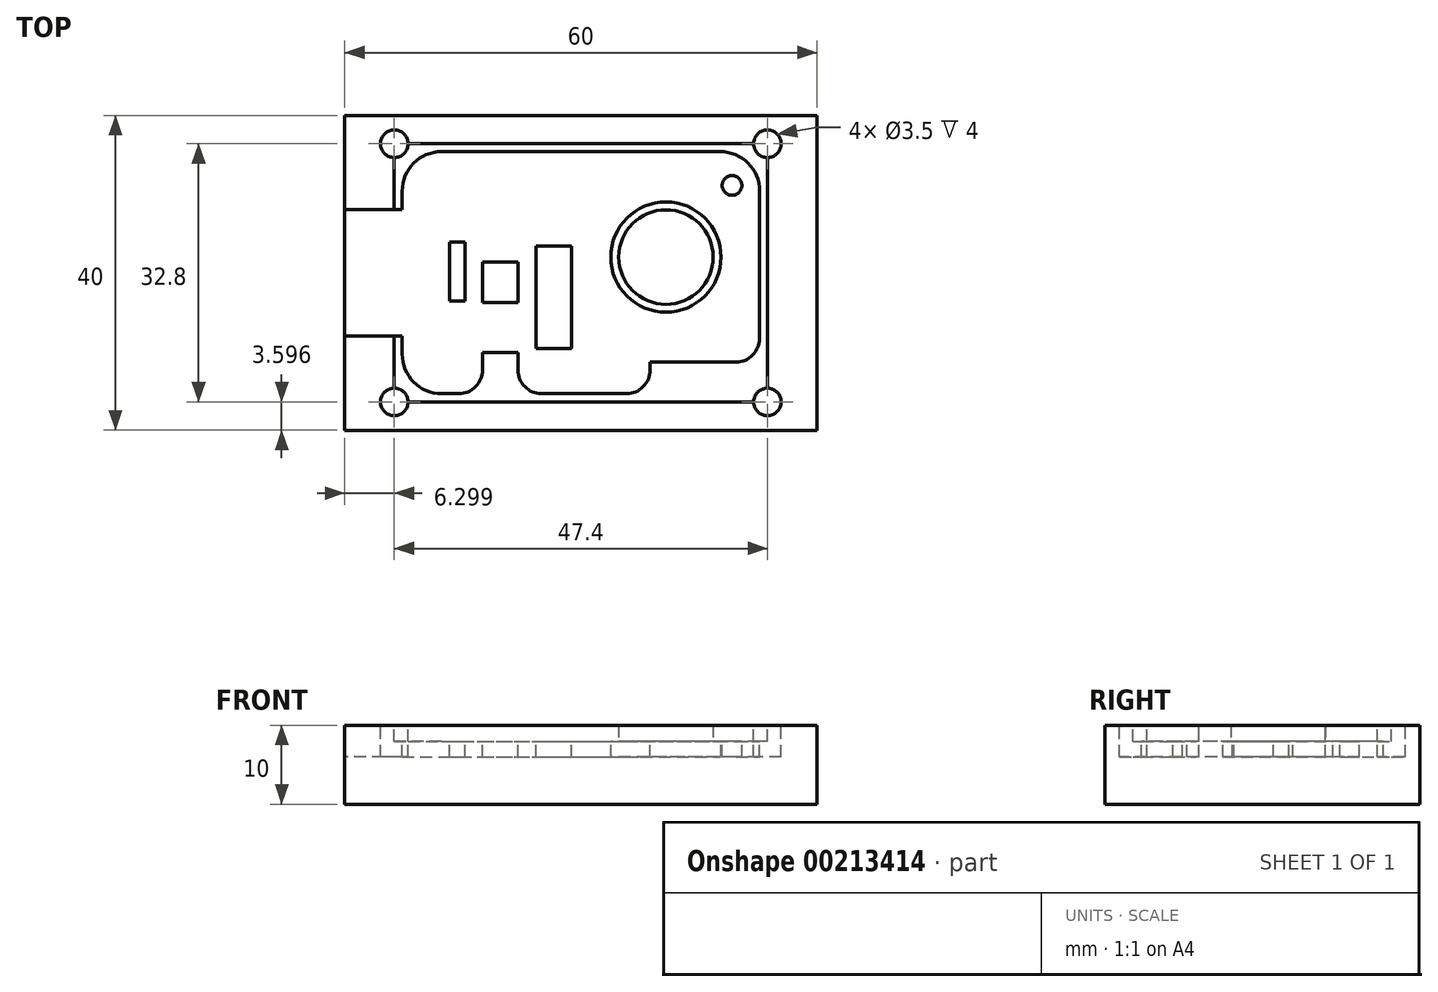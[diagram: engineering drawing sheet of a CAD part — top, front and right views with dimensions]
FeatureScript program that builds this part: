
annotation { "Feature Type Name" : "Feature", "Feature Type Description" : "" }
export const myFeature = defineFeature(function(context is Context, id is Id, definition is map)
    precondition{}
    {
        {
            var Q0;
            Q0=qCreatedBy(makeId("Top.planeOp"),FACE);
            var sketch = newSketch(context, id + "F0", { "sketchPlane" : qUnion([Q0])});
            skLineSegment(sketch, "E0.bottom", {"start": v(30.43, -28.68) * mm, "end": v(90.43, -28.68) * mm});
            skLineSegment(sketch, "E0.top", {"start": v(30.43, -68.68) * mm, "end": v(90.43, -68.68) * mm});
            skLineSegment(sketch, "E0.left", {"start": v(30.43, -28.68) * mm, "end": v(30.43, -68.68) * mm});
            skLineSegment(sketch, "E0.right", {"start": v(90.43, -28.68) * mm, "end": v(90.43, -68.68) * mm});
            skSolve(sketch);
        }
        {
            var Q0;
            Q0=makeQuery(id+"F0.imprint","IMPRINT",FACE,{"disambiguationData":[TD([[makeQuery(id+"F0.imprint","IMPRINT",EDGE,{"derivedFrom":sQuery(id+"F0.wireOp",EDGE,"E0.bottom")}),-1.0]])]});
            extrude(context, id + "F1", {"entities" : qUnion([Q0]), "depth" : 10 * mm});
        }
        {
            var Q0;
            Q0=makeQuery(id+"F1.opExtrude","CAP_FACE",FACE,{"disambiguationData":[OSD([sQuery(id+"F0.wireOp",EDGE,"E0.bottom"),sQuery(id+"F0.wireOp",EDGE,"E0.top"),sQuery(id+"F0.wireOp",EDGE,"E0.left"),sQuery(id+"F0.wireOp",EDGE,"E0.right")])],"isStart":false});
            var sketch = newSketch(context, id + "F2", { "sketchPlane" : qUnion([Q0])});
            skLineSegment(sketch, "E1.bottom", {"start": v(36.73, -32.28) * mm, "end": v(84.13, -32.28) * mm});
            skLineSegment(sketch, "E1.top", {"start": v(36.73, -65.08) * mm, "end": v(84.13, -65.08) * mm});
            skLineSegment(sketch, "E1.left", {"start": v(36.73, -32.28) * mm, "end": v(36.73, -65.08) * mm});
            skLineSegment(sketch, "E1.right", {"start": v(84.13, -32.28) * mm, "end": v(84.13, -65.08) * mm});
            skCircle(sketch, "E2", {"center": v(36.73, -32.28) * mm, "radius": 1.75 * mm});
            skCircle(sketch, "E3", {"center": v(84.13, -65.08) * mm, "radius": 1.75 * mm});
            skCircle(sketch, "E4", {"center": v(84.13, -32.28) * mm, "radius": 1.75 * mm});
            skCircle(sketch, "E5", {"center": v(36.73, -65.08) * mm, "radius": 1.75 * mm});
            skLineSegment(sketch, "E6.bottom", {"start": v(38.7, -40.66) * mm, "end": v(22.17, -40.66) * mm});
            skLineSegment(sketch, "E6.top", {"start": v(38.7, -56.7) * mm, "end": v(22.17, -56.7) * mm});
            skLineSegment(sketch, "E6.left", {"start": v(38.7, -40.66) * mm, "end": v(38.7, -56.7) * mm});
            skLineSegment(sketch, "E6.right", {"start": v(22.17, -40.66) * mm, "end": v(22.17, -56.7) * mm});
            skPoint(sketch, "E6.middle", {"position": v(30.43, -48.68) * mm});
            skSolve(sketch);
        }
        {
            var Q0;
            {var subQ0=sQuery(id+"F2.wireOp",EDGE,"E1.left");var subQ1=sQuery(id+"F2.wireOp",EDGE,"E1.bottom");var subQ2=makeQuery(id+"F2.imprint","INTERSECT",VERTEX,{"derivedFrom":[subQ1,subQ0]});Q0=makeQuery(id+"F2.imprint","IMPRINT",FACE,{"disambiguationData":[TD([[makeQuery(id+"F2.imprint","IMPRINT",EDGE,{"disambiguationData":[TD([[subQ2,-1.0]])],"derivedFrom":subQ1}),-1.0]])]});}
            var Q1;
            {var subQ0=sQuery(id+"F2.wireOp",EDGE,"E1.left");var subQ1=sQuery(id+"F2.wireOp",EDGE,"E1.bottom");var subQ2=makeQuery(id+"F2.imprint","INTERSECT",VERTEX,{"derivedFrom":[subQ1,subQ0]});Q1=makeQuery(id+"F2.imprint","IMPRINT",FACE,{"disambiguationData":[TD([[makeQuery(id+"F2.imprint","IMPRINT",EDGE,{"disambiguationData":[TD([[subQ2,-1.0]])],"derivedFrom":subQ1}),1.0]])]});}
            var Q2;
            {var subQ0=sQuery(id+"F2.wireOp",EDGE,"E1.left");var subQ1=sQuery(id+"F2.wireOp",EDGE,"E1.top");var subQ2=makeQuery(id+"F2.imprint","INTERSECT",VERTEX,{"derivedFrom":[subQ1,subQ0]});Q2=makeQuery(id+"F2.imprint","IMPRINT",FACE,{"disambiguationData":[TD([[makeQuery(id+"F2.imprint","IMPRINT",EDGE,{"disambiguationData":[TD([[subQ2,-1.0]])],"derivedFrom":subQ1}),1.0]])]});}
            var Q3;
            {var subQ0=sQuery(id+"F2.wireOp",EDGE,"E1.left");var subQ1=sQuery(id+"F2.wireOp",EDGE,"E1.top");var subQ2=makeQuery(id+"F2.imprint","INTERSECT",VERTEX,{"derivedFrom":[subQ1,subQ0]});Q3=makeQuery(id+"F2.imprint","IMPRINT",FACE,{"disambiguationData":[TD([[makeQuery(id+"F2.imprint","IMPRINT",EDGE,{"disambiguationData":[TD([[subQ2,-1.0]])],"derivedFrom":subQ1}),-1.0]])]});}
            var Q4;
            {var subQ0=sQuery(id+"F2.wireOp",EDGE,"E1.right");var subQ1=sQuery(id+"F2.wireOp",EDGE,"E1.top");var subQ2=makeQuery(id+"F2.imprint","INTERSECT",VERTEX,{"derivedFrom":[subQ1,subQ0]});Q4=makeQuery(id+"F2.imprint","IMPRINT",FACE,{"disambiguationData":[TD([[makeQuery(id+"F2.imprint","IMPRINT",EDGE,{"disambiguationData":[TD([[subQ2,1.0]])],"derivedFrom":subQ1}),-1.0]])]});}
            var Q5;
            {var subQ0=sQuery(id+"F2.wireOp",EDGE,"E1.right");var subQ1=sQuery(id+"F2.wireOp",EDGE,"E1.top");var subQ2=makeQuery(id+"F2.imprint","INTERSECT",VERTEX,{"derivedFrom":[subQ1,subQ0]});Q5=makeQuery(id+"F2.imprint","IMPRINT",FACE,{"disambiguationData":[TD([[makeQuery(id+"F2.imprint","IMPRINT",EDGE,{"disambiguationData":[TD([[subQ2,1.0]])],"derivedFrom":subQ1}),1.0]])]});}
            var Q6;
            {var subQ0=sQuery(id+"F2.wireOp",EDGE,"E2");var subQ13=sQuery(id+"F2.wireOp",EDGE,"E1.bottom");var subQ15=makeQuery(id+"F2.imprint","INTERSECT",VERTEX,{"derivedFrom":[subQ13,subQ0]});Q6=makeQuery(id+"F2.imprint","IMPRINT",FACE,{"disambiguationData":[TD([[makeQuery(id+"F2.imprint","IMPRINT",EDGE,{"disambiguationData":[TD([[subQ15,-1.0]])],"derivedFrom":subQ13}),-1.0]])]});}
            var Q7;
            {var subQ0=sQuery(id+"F2.wireOp",EDGE,"E1.right");var subQ1=sQuery(id+"F2.wireOp",EDGE,"E1.bottom");var subQ2=makeQuery(id+"F2.imprint","INTERSECT",VERTEX,{"derivedFrom":[subQ1,subQ0]});Q7=makeQuery(id+"F2.imprint","IMPRINT",FACE,{"disambiguationData":[TD([[makeQuery(id+"F2.imprint","IMPRINT",EDGE,{"disambiguationData":[TD([[subQ2,1.0]])],"derivedFrom":subQ1}),-1.0]])]});}
            var Q8;
            {var subQ0=sQuery(id+"F2.wireOp",EDGE,"E1.right");var subQ1=sQuery(id+"F2.wireOp",EDGE,"E1.bottom");var subQ2=makeQuery(id+"F2.imprint","INTERSECT",VERTEX,{"derivedFrom":[subQ1,subQ0]});Q8=makeQuery(id+"F2.imprint","IMPRINT",FACE,{"disambiguationData":[TD([[makeQuery(id+"F2.imprint","IMPRINT",EDGE,{"disambiguationData":[TD([[subQ2,1.0]])],"derivedFrom":subQ1}),1.0]])]});}
            extrude(context, id + "F3", {"entities" : qUnion([Q0, Q1, Q2, Q3, Q4, Q5, Q6, Q7, Q8]), "operationType" : NewBodyOperationType.REMOVE, "oppositeDirection" : true, "depth" : 2 * mm});
        }
        {
            var Q0;
            Q0=makeQuery(id+"F3.boolean.opBoolean","COPY",FACE,{"derivedFrom":makeQuery(id+"F3.opExtrude","CAP_FACE",FACE,{"disambiguationData":[OSD([sQuery(id+"F2.wireOp",EDGE,"E1.bottom"),sQuery(id+"F2.wireOp",EDGE,"E1.top"),sQuery(id+"F2.wireOp",EDGE,"E1.left"),sQuery(id+"F2.wireOp",EDGE,"E1.right"),sQuery(id+"F2.wireOp",EDGE,"E2"),sQuery(id+"F2.wireOp",EDGE,"E3"),sQuery(id+"F2.wireOp",EDGE,"E4"),sQuery(id+"F2.wireOp",EDGE,"E5")])],"isStart":false})});
            var sketch = newSketch(context, id + "F4", { "sketchPlane" : qUnion([Q0])});
            skCircle(sketch, "E7", {"center": v(71.23, -46.68) * mm, "radius": 6 * mm});
            skCircle(sketch, "E8", {"center": v(79.63, -37.58) * mm, "radius": 1.25 * mm});
            skLineSegment(sketch, "E9.bottom", {"start": v(42.73, -33.28) * mm, "end": v(78.13, -33.28) * mm});
            skLineSegment(sketch, "E9.left", {"start": v(37.73, -38.28) * mm, "end": v(37.73, -59.03) * mm});
            skLineSegment(sketch, "E9.right", {"start": v(83.13, -38.28) * mm, "end": v(83.13, -57.03) * mm});
            skLineSegment(sketch, "E10.bottom", {"start": v(47.93, -47.28) * mm, "end": v(52.43, -47.28) * mm});
            skLineSegment(sketch, "E10.top", {"start": v(47.93, -52.48) * mm, "end": v(52.43, -52.48) * mm});
            skLineSegment(sketch, "E10.left", {"start": v(47.93, -47.28) * mm, "end": v(47.93, -52.48) * mm});
            skLineSegment(sketch, "E10.right", {"start": v(52.43, -47.28) * mm, "end": v(52.43, -52.48) * mm});
            skLineSegment(sketch, "E11.bottom", {"start": v(47.93, -58.83) * mm, "end": v(52.43, -58.83) * mm});
            skLineSegment(sketch, "E11.left", {"start": v(47.93, -58.83) * mm, "end": v(47.93, -61.03) * mm});
            skLineSegment(sketch, "E11.right", {"start": v(52.43, -58.83) * mm, "end": v(52.43, -61.03) * mm});
            skPoint(sketch, "E12.visualSharp", {"position": v(37.73, -33.28) * mm});
            skArc(sketch, "E12.filletArc", {"start": v(42.73, -33.28) * mm, "mid": v(39.2, -34.75) * mm, "end": v(37.73, -38.28) * mm});
            skPoint(sketch, "E13.visualSharp", {"position": v(83.13, -33.28) * mm});
            skArc(sketch, "E13.filletArc", {"start": v(83.13, -38.28) * mm, "mid": v(81.66, -34.75) * mm, "end": v(78.13, -33.28) * mm});
            skPoint(sketch, "E14.visualSharp", {"position": v(83.13, -64.03) * mm});
            skPoint(sketch, "E15.visualSharp", {"position": v(37.73, -64.03) * mm});
            skArc(sketch, "E15.filletArc", {"start": v(37.73, -59.03) * mm, "mid": v(39.2, -62.56) * mm, "end": v(42.73, -64.03) * mm});
            skLineSegment(sketch, "E16", {"start": v(42.73, -64.03) * mm, "end": v(44.93, -64.03) * mm});
            skPoint(sketch, "E17.visualSharp", {"position": v(47.93, -64.03) * mm});
            skArc(sketch, "E17.filletArc", {"start": v(44.93, -64.03) * mm, "mid": v(47.05, -63.15) * mm, "end": v(47.93, -61.03) * mm});
            skPoint(sketch, "E18.visualSharp", {"position": v(52.43, -64.03) * mm});
            skArc(sketch, "E18.filletArc", {"start": v(52.43, -61.03) * mm, "mid": v(53.3, -63.15) * mm, "end": v(55.43, -64.03) * mm});
            skLineSegment(sketch, "E19.top", {"start": v(80.13, -60.03) * mm, "end": v(69.23, -60.03) * mm});
            skLineSegment(sketch, "E19.right", {"start": v(69.23, -61.03) * mm, "end": v(69.23, -60.03) * mm});
            skLineSegment(sketch, "E20", {"start": v(55.43, -64.03) * mm, "end": v(66.23, -64.03) * mm});
            skLineSegment(sketch, "E21.bottom", {"start": v(54.73, -45.28) * mm, "end": v(59.23, -45.28) * mm});
            skLineSegment(sketch, "E21.top", {"start": v(54.73, -58.28) * mm, "end": v(59.23, -58.28) * mm});
            skLineSegment(sketch, "E21.left", {"start": v(54.73, -45.28) * mm, "end": v(54.73, -58.28) * mm});
            skLineSegment(sketch, "E21.right", {"start": v(59.23, -45.28) * mm, "end": v(59.23, -58.28) * mm});
            skLineSegment(sketch, "E22.bottom", {"start": v(43.73, -44.78) * mm, "end": v(45.73, -44.78) * mm});
            skLineSegment(sketch, "E22.top", {"start": v(43.73, -52.28) * mm, "end": v(45.73, -52.28) * mm});
            skLineSegment(sketch, "E22.left", {"start": v(43.73, -44.78) * mm, "end": v(43.73, -52.28) * mm});
            skLineSegment(sketch, "E22.right", {"start": v(45.73, -44.78) * mm, "end": v(45.73, -52.28) * mm});
            skPoint(sketch, "E23.visualSharp", {"position": v(69.23, -64.03) * mm});
            skArc(sketch, "E23.filletArc", {"start": v(66.23, -64.03) * mm, "mid": v(68.35, -63.15) * mm, "end": v(69.23, -61.03) * mm});
            skPoint(sketch, "E24.visualSharp", {"position": v(83.13, -60.03) * mm});
            skArc(sketch, "E24.filletArc", {"start": v(80.13, -60.03) * mm, "mid": v(82.25, -59.15) * mm, "end": v(83.13, -57.03) * mm});
            skCircle(sketch, "E25", {"center": v(71.23, -46.68) * mm, "radius": 7 * mm});
            skSolve(sketch);
        }
        {
            var Q0;
            {var subQ0=sQuery(id+"F2.wireOp",EDGE,"E1.left");var subQ1=sQuery(id+"F2.wireOp",EDGE,"E1.bottom");var subQ2=makeQuery(id+"F2.imprint","INTERSECT",VERTEX,{"derivedFrom":[subQ1,subQ0]});Q0=makeQuery(id+"F2.imprint","IMPRINT",FACE,{"disambiguationData":[TD([[makeQuery(id+"F2.imprint","IMPRINT",EDGE,{"disambiguationData":[TD([[subQ2,-1.0]])],"derivedFrom":subQ1}),-1.0]])]});}
            var Q1;
            {var subQ0=sQuery(id+"F2.wireOp",EDGE,"E1.left");var subQ1=sQuery(id+"F2.wireOp",EDGE,"E1.bottom");var subQ2=makeQuery(id+"F2.imprint","INTERSECT",VERTEX,{"derivedFrom":[subQ1,subQ0]});Q1=makeQuery(id+"F2.imprint","IMPRINT",FACE,{"disambiguationData":[TD([[makeQuery(id+"F2.imprint","IMPRINT",EDGE,{"disambiguationData":[TD([[subQ2,-1.0]])],"derivedFrom":subQ1}),1.0]])]});}
            var Q2;
            {var subQ0=sQuery(id+"F2.wireOp",EDGE,"E1.left");var subQ1=sQuery(id+"F2.wireOp",EDGE,"E1.top");var subQ2=makeQuery(id+"F2.imprint","INTERSECT",VERTEX,{"derivedFrom":[subQ1,subQ0]});Q2=makeQuery(id+"F2.imprint","IMPRINT",FACE,{"disambiguationData":[TD([[makeQuery(id+"F2.imprint","IMPRINT",EDGE,{"disambiguationData":[TD([[subQ2,-1.0]])],"derivedFrom":subQ1}),1.0]])]});}
            var Q3;
            {var subQ0=sQuery(id+"F2.wireOp",EDGE,"E1.left");var subQ1=sQuery(id+"F2.wireOp",EDGE,"E1.top");var subQ2=makeQuery(id+"F2.imprint","INTERSECT",VERTEX,{"derivedFrom":[subQ1,subQ0]});Q3=makeQuery(id+"F2.imprint","IMPRINT",FACE,{"disambiguationData":[TD([[makeQuery(id+"F2.imprint","IMPRINT",EDGE,{"disambiguationData":[TD([[subQ2,-1.0]])],"derivedFrom":subQ1}),-1.0]])]});}
            var Q4;
            {var subQ0=sQuery(id+"F2.wireOp",EDGE,"E1.right");var subQ1=sQuery(id+"F2.wireOp",EDGE,"E1.bottom");var subQ2=makeQuery(id+"F2.imprint","INTERSECT",VERTEX,{"derivedFrom":[subQ1,subQ0]});Q4=makeQuery(id+"F2.imprint","IMPRINT",FACE,{"disambiguationData":[TD([[makeQuery(id+"F2.imprint","IMPRINT",EDGE,{"disambiguationData":[TD([[subQ2,1.0]])],"derivedFrom":subQ1}),-1.0]])]});}
            var Q5;
            {var subQ0=sQuery(id+"F2.wireOp",EDGE,"E1.right");var subQ1=sQuery(id+"F2.wireOp",EDGE,"E1.bottom");var subQ2=makeQuery(id+"F2.imprint","INTERSECT",VERTEX,{"derivedFrom":[subQ1,subQ0]});Q5=makeQuery(id+"F2.imprint","IMPRINT",FACE,{"disambiguationData":[TD([[makeQuery(id+"F2.imprint","IMPRINT",EDGE,{"disambiguationData":[TD([[subQ2,1.0]])],"derivedFrom":subQ1}),1.0]])]});}
            var Q6;
            {var subQ0=sQuery(id+"F2.wireOp",EDGE,"E1.right");var subQ1=sQuery(id+"F2.wireOp",EDGE,"E1.top");var subQ2=makeQuery(id+"F2.imprint","INTERSECT",VERTEX,{"derivedFrom":[subQ1,subQ0]});Q6=makeQuery(id+"F2.imprint","IMPRINT",FACE,{"disambiguationData":[TD([[makeQuery(id+"F2.imprint","IMPRINT",EDGE,{"disambiguationData":[TD([[subQ2,1.0]])],"derivedFrom":subQ1}),1.0]])]});}
            var Q7;
            {var subQ0=sQuery(id+"F2.wireOp",EDGE,"E1.right");var subQ1=sQuery(id+"F2.wireOp",EDGE,"E1.top");var subQ2=makeQuery(id+"F2.imprint","INTERSECT",VERTEX,{"derivedFrom":[subQ1,subQ0]});Q7=makeQuery(id+"F2.imprint","IMPRINT",FACE,{"disambiguationData":[TD([[makeQuery(id+"F2.imprint","IMPRINT",EDGE,{"disambiguationData":[TD([[subQ2,1.0]])],"derivedFrom":subQ1}),-1.0]])]});}
            extrude(context, id + "F5", {"entities" : qUnion([Q0, Q1, Q2, Q3, Q4, Q5, Q6, Q7]), "operationType" : NewBodyOperationType.REMOVE, "oppositeDirection" : true, "depth" : 4 * mm});
        }
        {
            var Q0;
            Q0=makeQuery(id+"F4.imprint","IMPRINT",FACE,{"disambiguationData":[TD([[makeQuery(id+"F4.imprint","IMPRINT",EDGE,{"derivedFrom":sQuery(id+"F4.wireOp",EDGE,"E7")}),1.0]])]});
            extrude(context, id + "F6", {"entities" : qUnion([Q0]), "operationType" : NewBodyOperationType.ADD, "depth" : 2 * mm});
        }
        {
            var Q0;
            {var subQ0=sQuery(id+"F2.wireOp",EDGE,"E6.bottom");var subQ1=sQuery(id+"F2.wireOp",EDGE,"E1.left");var subQ2=makeQuery(id+"F2.imprint","INTERSECT",VERTEX,{"derivedFrom":[subQ1,subQ0]});Q0=makeQuery(id+"F2.imprint","IMPRINT",FACE,{"disambiguationData":[TD([[makeQuery(id+"F2.imprint","IMPRINT",EDGE,{"disambiguationData":[TD([[subQ2,-1.0]])],"derivedFrom":subQ1}),-1.0]])]});}
            var Q1;
            {var subQ5=sQuery(id+"F2.wireOp",EDGE,"E6.left");Q1=makeQuery(id+"F2.imprint","IMPRINT",FACE,{"disambiguationData":[TD([[makeQuery(id+"F2.imprint","IMPRINT",EDGE,{"derivedFrom":subQ5}),-1.0]])]});}
            extrude(context, id + "F7", {"entities" : qUnion([Q0, Q1]), "operationType" : NewBodyOperationType.REMOVE, "oppositeDirection" : true, "depth" : 4 * mm});
        }
        {
            var Q0;
            Q0=makeQuery(id+"F4.imprint","IMPRINT",FACE,{"disambiguationData":[TD([[makeQuery(id+"F4.imprint","IMPRINT",EDGE,{"derivedFrom":sQuery(id+"F4.wireOp",EDGE,"E8")}),-1.0]])]});
            extrude(context, id + "F8", {"entities" : qUnion([Q0]), "operationType" : NewBodyOperationType.REMOVE, "oppositeDirection" : true, "depth" : 2 * mm});
        }
    });
